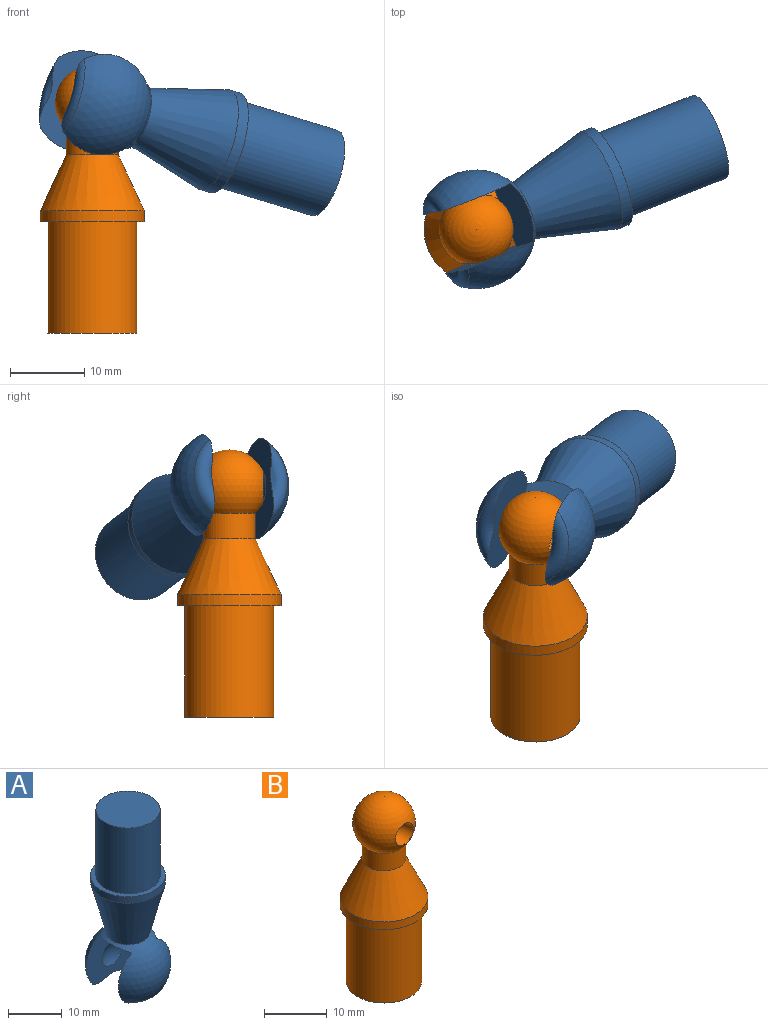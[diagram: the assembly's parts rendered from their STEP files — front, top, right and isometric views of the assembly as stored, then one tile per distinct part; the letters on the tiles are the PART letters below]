
ASSEMBLY  parts=2 mates=1
PART A: 15 faces, bbox 16x16x40.1 mm
  f0: torus R=5.43mm, axis (0,0,1), area 20.5mm2, adj f1,f11
  f1: sphere r=8mm, area 350.2mm2, adj f0,f2,f3,f8,f9,f10,f11
  f2: torus R=5.43mm, axis (0,0,1), area 20.5mm2, adj f1,f10
  f3: cone r=7mm half-angle=14.5deg, axis (0,0,1), area 413.1mm2, adj f1,f4
  f4: cylinder r=7mm len=14mm, axis (0,0,1), area 66mm2, adj f3,f5
  f5: plane 14x14mm, normal (0,0,1), area 40.8mm2, adj f4,f6
  f6: cylinder r=6mm len=15mm, axis (0,0,1), area 565.5mm2, adj f5,f7
  f7: plane 12x12mm, normal (0,0,1), area 113.1mm2, adj f6
  f8: plane 8.5x4.59mm, normal (0.42,0,-0.91), area 35.4mm2, adj f1,f9,f10,f11,f14
  f9: plane 8.5x4.59mm, normal (-0.42,0,-0.91), area 35.4mm2, adj f1,f8,f10,f11,f14
  f10: plane 13.56x11.01mm, normal (0,1,0), area 101.2mm2, adj f1,f2,f8,f9,f13
  f11: plane 13.56x11.01mm, normal (0,-1,0), area 101.2mm2, adj f0,f1,f8,f9,f12
  f12: sphere r=5mm, area 23.6mm2, adj f11
  f13: sphere r=5mm, area 23.6mm2, adj f10
  f14: sphere r=5mm, area 6.9mm2, adj f8,f9
PART B: 8 faces, bbox 18.1x33.5x40.1 mm
  f0: sphere r=5mm, area 243mm2, adj f5,f7
  f1: cylinder r=6mm len=15mm, axis (0,0,1), area 565.5mm2, adj f2,f6
  f2: plane 14x14mm, normal (0,0,-1), area 40.8mm2, adj f1,f3
  f3: cylinder r=7mm len=14mm, axis (0,0,1), area 66mm2, adj f2,f4
  f4: cone r=3.5mm half-angle=25deg, axis (0,0,-1), area 273mm2, adj f3,f5
  f5: cylinder r=3.5mm len=7mm, axis (0,0,1), area 75.4mm2, adj f0,f4
  f6: plane 12x12mm, normal (0,0,-1), area 113.1mm2, adj f1
  f7: torus R=25.11mm, axis (0,1,0), area 98.5mm2, adj f0
PLACE A rot(axis=(-0.16,0.97,0.16),107.7deg) t=(-14.32,-5.69,20.32)mm
PLACE B at identity fixed
MATE ball B.f1 <-> A.f4  axis (0,0,1) through (0,0,16)mm
